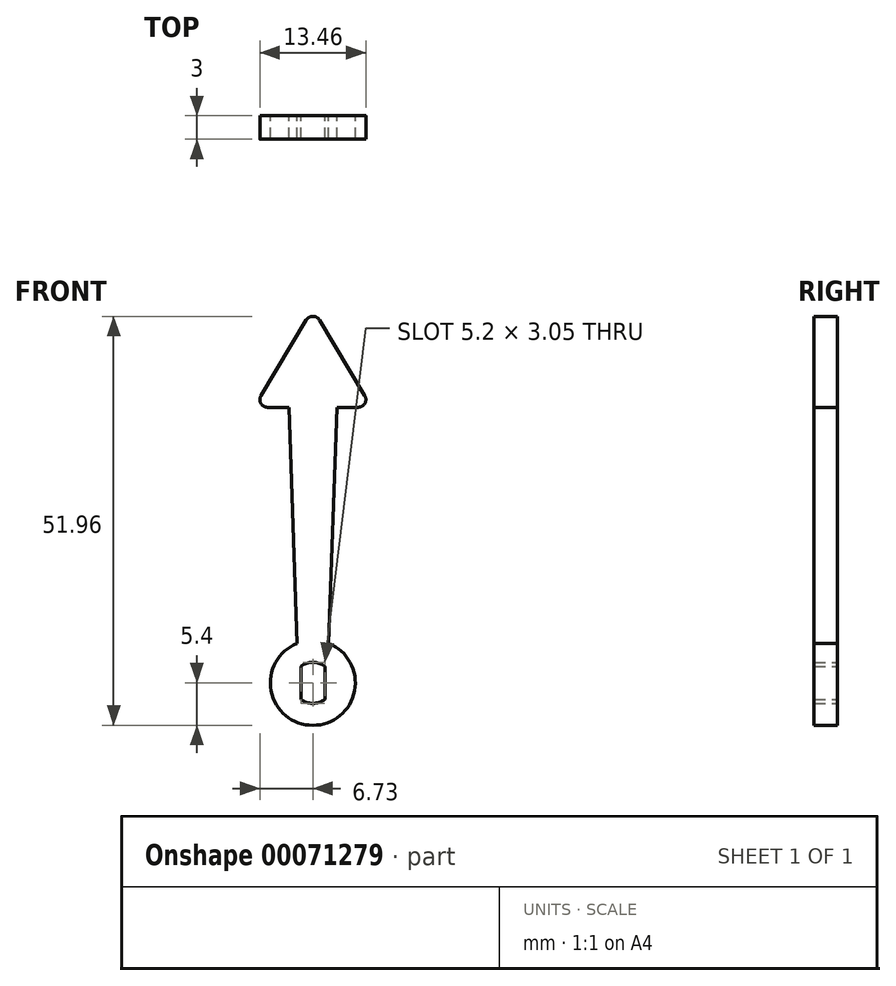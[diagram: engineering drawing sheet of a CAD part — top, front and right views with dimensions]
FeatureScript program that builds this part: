
annotation { "Feature Type Name" : "Feature", "Feature Type Description" : "" }
export const myFeature = defineFeature(function(context is Context, id is Id, definition is map)
    precondition{}
    {
        {
            var Q0;
            Q0=qCreatedBy(makeId("Front.planeOp"),FACE);
            var sketch = newSketch(context, id + "F0", { "sketchPlane" : qUnion([Q0])});
            skPoint(sketch, "E0.rect.middle", {"position": v(0, 0) * mm});
            skCircle(sketch, "E1", {"center": v(0, 0) * mm, "radius": 5.4 * mm});
            skCircle(sketch, "E2", {"center": v(0, 0) * mm, "radius": 2.6 * mm});
            skLineSegment(sketch, "E3", {"start": v(-1.53, 2.1) * mm, "end": v(-1.53, -2.1) * mm});
            skLineSegment(sketch, "E4", {"start": v(1.52, 2.1) * mm, "end": v(1.52, -2.1) * mm});
            skLineSegment(sketch, "E5", {"start": v(0, 0) * mm, "end": v(0, 35) * mm, "construction": true});
            skLineSegment(sketch, "E6", {"start": v(0, 35) * mm, "end": v(3.05, 35) * mm});
            skLineSegment(sketch, "E7", {"start": v(3.05, 35) * mm, "end": v(2, 5.02) * mm});
            skLineSegment(sketch, "E8", {"start": v(2, 5.02) * mm, "end": v(0, 5.02) * mm});
            skLineSegment(sketch, "E9.MirrorCS", {"start": v(-2, 5.02) * mm, "end": v(0, 5.02) * mm});
            skLineSegment(sketch, "E10.MirrorCS", {"start": v(0, 35) * mm, "end": v(-3.05, 35) * mm});
            skLineSegment(sketch, "E11.MirrorCS", {"start": v(-3.05, 35) * mm, "end": v(-2, 5.02) * mm});
            skLineSegment(sketch, "E12", {"start": v(0, 35) * mm, "end": v(0, 47.5) * mm, "construction": true});
            skLineSegment(sketch, "E13", {"start": v(0, 35) * mm, "end": v(7.5, 35) * mm});
            skLineSegment(sketch, "E14", {"start": v(7.5, 35) * mm, "end": v(0, 47.5) * mm});
            skLineSegment(sketch, "E15.MirrorCS", {"start": v(-7.5, 35) * mm, "end": v(0, 47.5) * mm});
            skLineSegment(sketch, "E16.MirrorCS", {"start": v(0, 35) * mm, "end": v(-7.5, 35) * mm});
            skSolve(sketch);
        }
        {
            var Q0;
            Q0 = qSketchRegion(id + "F0", true);
            var Q1;
            {var subQ0=sQuery(id+"F0.wireOp",EDGE,"E4");Q1=makeQuery(id+"F0.imprint","IMPRINT",FACE,{"disambiguationData":[TD([[makeQuery(id+"F0.imprint","IMPRINT",EDGE,{"derivedFrom":subQ0}),1.0]])]});}
            var Q2;
            {var subQ0=sQuery(id+"F0.wireOp",EDGE,"E3");Q2=makeQuery(id+"F0.imprint","IMPRINT",FACE,{"disambiguationData":[TD([[makeQuery(id+"F0.imprint","IMPRINT",EDGE,{"derivedFrom":subQ0}),-1.0]])]});}
            extrude(context, id + "F1", {"entities" : qUnion([Q0, Q1, Q2]), "depth" : 3 * mm});
        }
        {
            var Q0;
            Q0=makeQuery(id+"F1.opExtrude","SWEPT_EDGE",EDGE,{"disambiguationData":[OSD([sQuery(id+"F0.wireOp",EDGE,"E14"),sQuery(id+"F0.wireOp",EDGE,"E15.MirrorCS")])]});
            fillet(context, id + "F2", {"entities" : qUnion([Q0]), "radius" : 1 * mm, "tangentPropagation" : true, "allowEdgeOverflow" : false});
        }
        {
            var Q0;
            Q0=makeQuery(id+"F1.opExtrude","SWEPT_EDGE",EDGE,{"disambiguationData":[OSD([sQuery(id+"F0.wireOp",EDGE,"E15.MirrorCS"),sQuery(id+"F0.wireOp",EDGE,"E16.MirrorCS")])]});
            fillet(context, id + "F3", {"entities" : qUnion([Q0]), "radius" : 1 * mm, "tangentPropagation" : true, "allowEdgeOverflow" : false});
        }
        {
            var Q0;
            Q0=makeQuery(id+"F1.opExtrude","SWEPT_EDGE",EDGE,{"disambiguationData":[OSD([sQuery(id+"F0.wireOp",EDGE,"E13"),sQuery(id+"F0.wireOp",EDGE,"E14")])]});
            fillet(context, id + "F4", {"entities" : qUnion([Q0]), "radius" : 1 * mm, "tangentPropagation" : true, "allowEdgeOverflow" : false});
        }
    });
